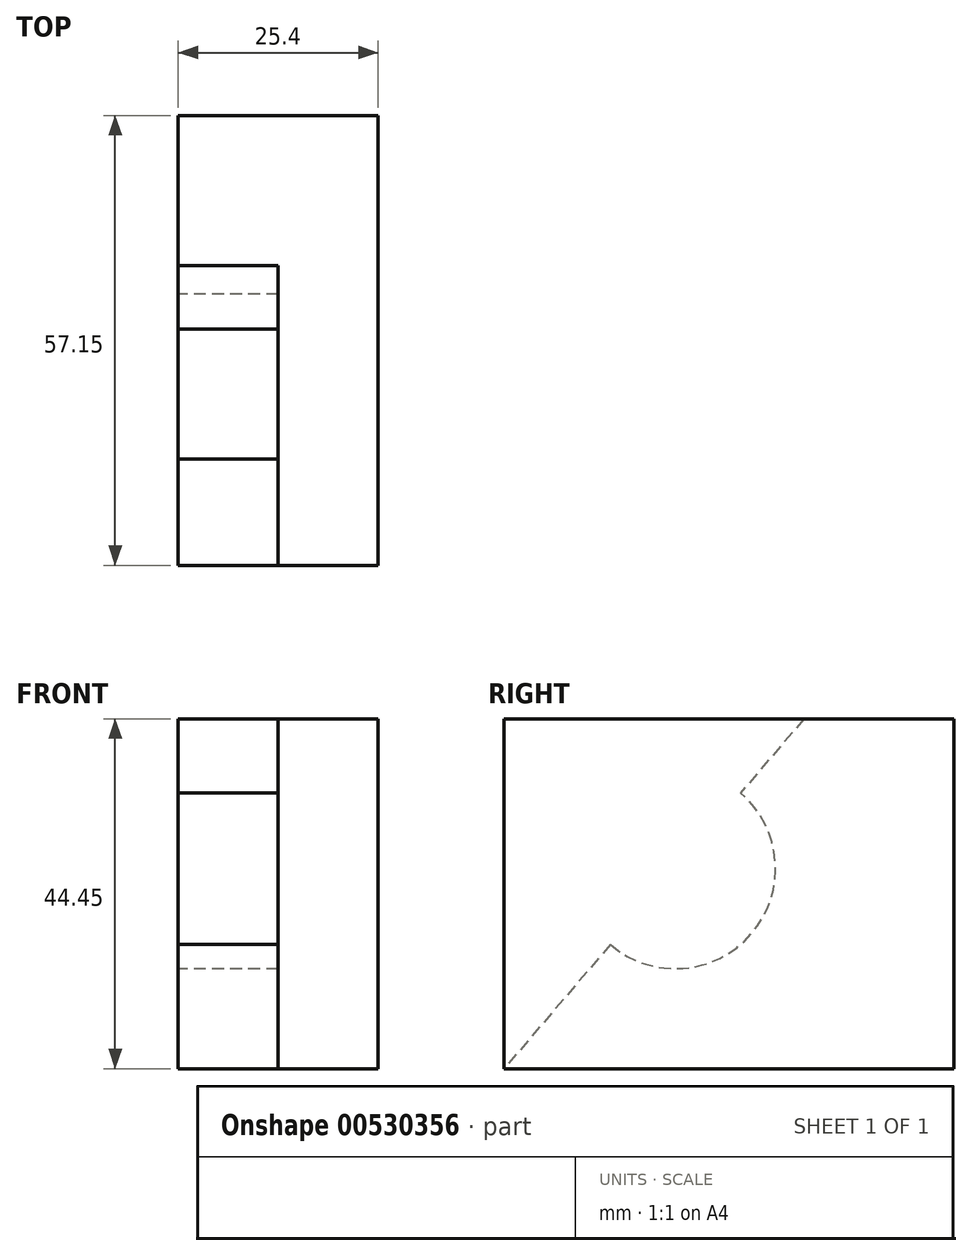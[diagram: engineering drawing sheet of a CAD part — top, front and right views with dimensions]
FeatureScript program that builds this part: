
annotation { "Feature Type Name" : "Feature", "Feature Type Description" : "" }
export const myFeature = defineFeature(function(context is Context, id is Id, definition is map)
    precondition{}
    {
        {
            var Q0;
            Q0=qCreatedBy(makeId("Front.planeOp"),FACE);
            var sketch = newSketch(context, id + "F0", { "sketchPlane" : qUnion([Q0])});
            skLineSegment(sketch, "E0", {"start": v(-25.4, 44.45) * mm, "end": v(-25.4, 0) * mm});
            skLineSegment(sketch, "E1", {"start": v(-25.4, 0) * mm, "end": v(0, 0) * mm});
            skLineSegment(sketch, "E2", {"start": v(0, 0) * mm, "end": v(0, 44.45) * mm});
            skLineSegment(sketch, "E3", {"start": v(0, 44.45) * mm, "end": v(-25.4, 44.45) * mm});
            skSolve(sketch);
        }
        {
            var Q0;
            Q0=makeQuery(id+"F0.imprint","IMPRINT",FACE,{"disambiguationData":[TD([[makeQuery(id+"F0.imprint","IMPRINT",EDGE,{"derivedFrom":sQuery(id+"F0.wireOp",EDGE,"E0")}),1.0]])]});
            extrude(context, id + "F1", {"entities" : qUnion([Q0]), "depth" : 57.15 * mm, "offsetDistance" : 25.4 * mm});
        }
        {
            var Q0;
            Q0=makeQuery(id+"F1.opExtrude","SWEPT_FACE",FACE,{"disambiguationData":[OSD([sQuery(id+"F0.wireOp",EDGE,"E0")])]});
            var sketch = newSketch(context, id + "F2", { "sketchPlane" : qUnion([Q0])});
            skLineSegment(sketch, "E4", {"start": v(19.05, 44.45) * mm, "end": v(57.15, 0) * mm});
            skSolve(sketch);
        }
        {
            var Q0;
            Q0 = qSketchRegion(id + "F2", true);
            var Q1;
            {var subQ0=sQuery(id+"F2.wireOp",EDGE,"E4");Q1=makeQuery(id+"F2.imprint","IMPRINT",FACE,{"disambiguationData":[TD([[makeQuery(id+"F2.imprint","IMPRINT",EDGE,{"derivedFrom":subQ0}),1.0]])]});}
            extrude(context, id + "F3", {"entities" : qUnion([Q0, Q1]), "operationType" : NewBodyOperationType.REMOVE, "oppositeDirection" : true, "depth" : 12.7 * mm, "offsetDistance" : 25.4 * mm});
        }
        {
            var Q0;
            Q0=makeQuery(id+"F1.opExtrude","SWEPT_FACE",FACE,{"disambiguationData":[OSD([sQuery(id+"F0.wireOp",EDGE,"E0")])]});
            var sketch = newSketch(context, id + "F4", { "sketchPlane" : qUnion([Q0])});
            skCircle(sketch, "E5", {"center": v(35.38, 25.4) * mm, "radius": 12.7 * mm});
            skSolve(sketch);
        }
        {
            var Q0;
            Q0 = qSketchRegion(id + "F4", true);
            extrude(context, id + "F5", {"entities" : qUnion([Q0]), "operationType" : NewBodyOperationType.REMOVE, "oppositeDirection" : true, "depth" : 12.7 * mm, "offsetDistance" : 25.4 * mm});
        }
    });
